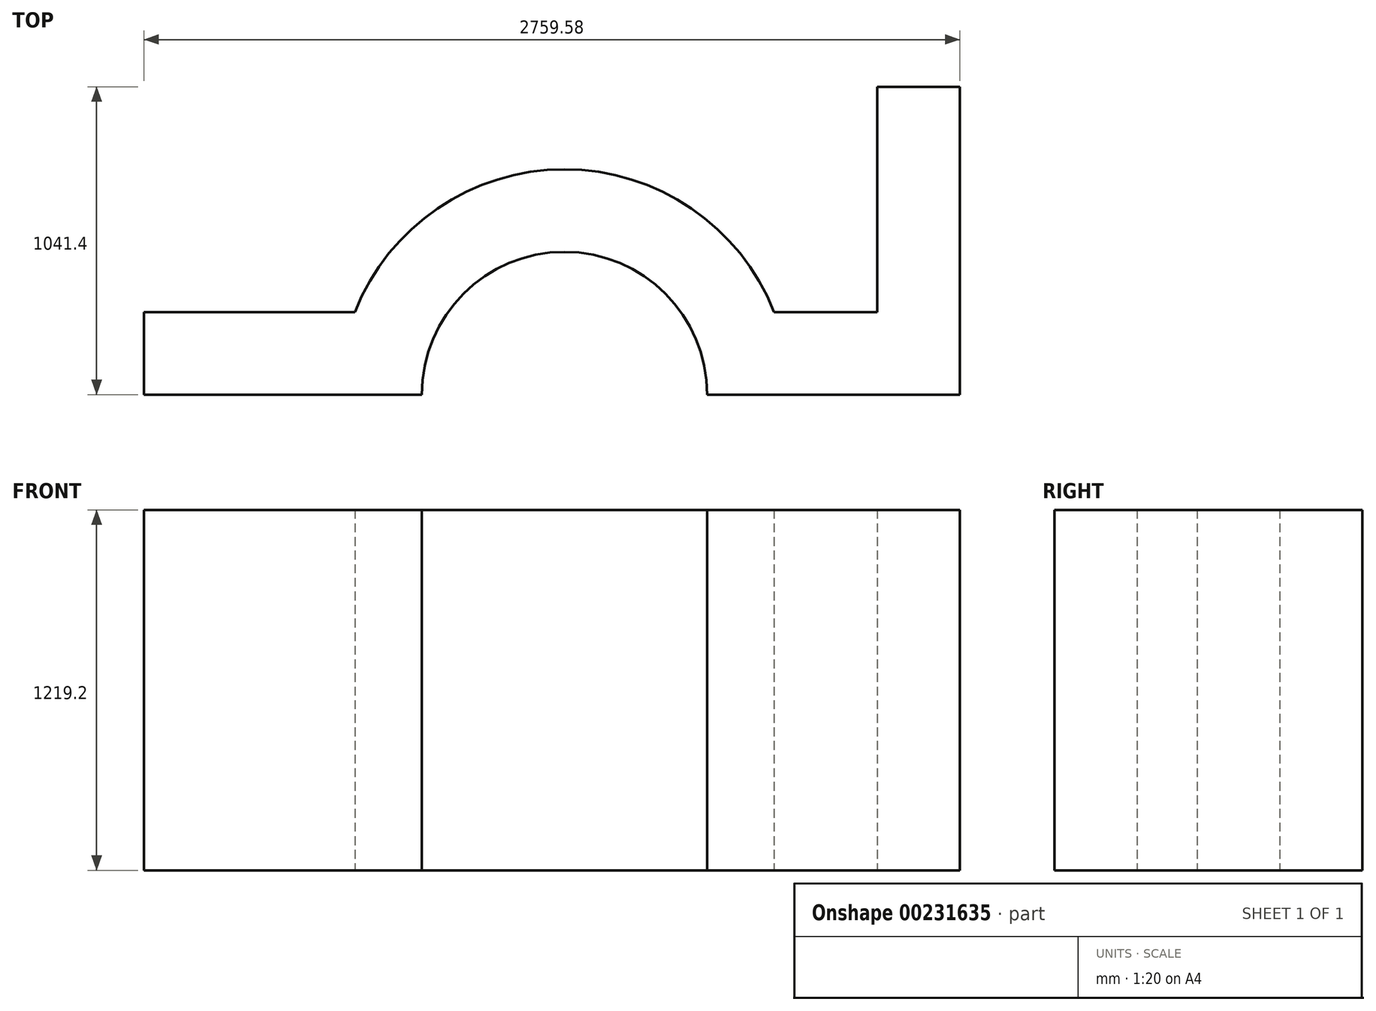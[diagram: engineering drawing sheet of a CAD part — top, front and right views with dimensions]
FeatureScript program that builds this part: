
annotation { "Feature Type Name" : "Feature", "Feature Type Description" : "" }
export const myFeature = defineFeature(function(context is Context, id is Id, definition is map)
    precondition{}
    {
        {
            var Q0;
            Q0=qCreatedBy(makeId("Top.planeOp"),FACE);
            var sketch = newSketch(context, id + "F0", { "sketchPlane" : qUnion([Q0])});
            skArc(sketch, "E0", {"start": v(762, 0) * mm, "mid": v(0, 762) * mm, "end": v(-762, 0) * mm});
            skArc(sketch, "E1", {"start": v(482.6, 0) * mm, "mid": v(0, 482.6) * mm, "end": v(-482.6, 0) * mm});
            skLineSegment(sketch, "E2.top", {"start": v(-393.5, 279.4) * mm, "end": v(-1422.4, 279.4) * mm});
            skLineSegment(sketch, "E2.right", {"start": v(-1422.4, 0) * mm, "end": v(-1422.4, 279.4) * mm});
            skLineSegment(sketch, "E3.top", {"start": v(708.93, 279.4) * mm, "end": v(1337.18, 279.4) * mm});
            skLineSegment(sketch, "E3.right", {"start": v(1337.18, 0) * mm, "end": v(1337.18, 279.4) * mm});
            skLineSegment(sketch, "E4.trimOffspring", {"start": v(482.6, 0) * mm, "end": v(1337.18, 0) * mm});
            skLineSegment(sketch, "E5.trimOffspring", {"start": v(-482.6, 0) * mm, "end": v(-1422.4, 0) * mm});
            skLineSegment(sketch, "E6.bottom", {"start": v(1337.18, 0) * mm, "end": v(1057.78, 0) * mm});
            skLineSegment(sketch, "E6.top", {"start": v(1337.18, 1041.4) * mm, "end": v(1057.78, 1041.4) * mm});
            skLineSegment(sketch, "E6.left", {"start": v(1337.18, 0) * mm, "end": v(1337.18, 1041.4) * mm});
            skLineSegment(sketch, "E6.right", {"start": v(1057.78, 0) * mm, "end": v(1057.78, 1041.4) * mm});
            skSolve(sketch);
        }
        {
            var Q0;
            Q0 = qSketchRegion(id + "F0", true);
            extrude(context, id + "F1", {"entities" : qUnion([Q0]), "depth" : 1219.2 * mm});
        }
        {
            var Q0;
            Q0=makeQuery(id+"F1.opExtrude","CAP_EDGE",EDGE,{"disambiguationData":[OSD([sQuery(id+"F0.wireOp",EDGE,"E0")])],"isStart":false});
            cPoint(context, id + "F2", {"entities" : qUnion([Q0]), "parameter" : 0.5});
        }
        {
            var Q0;
            Q0=qCreatedBy(makeId("Front.planeOp"),FACE);
            var Q1;
            Q1 = qCreatedBy(id + "F2" ,VERTEX);
            cPlane(context, id + "F3", {"entities" : qUnion([Q0, Q1]), "cplaneType" : CPlaneType.PLANE_POINT, "offset" : 0.03 * yard, "width" : 0.17 * yard, "height" : 0.17 * yard});
        }
    });
